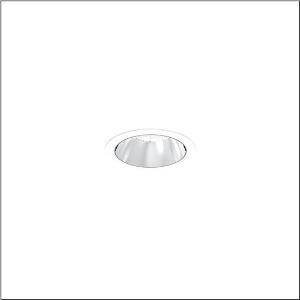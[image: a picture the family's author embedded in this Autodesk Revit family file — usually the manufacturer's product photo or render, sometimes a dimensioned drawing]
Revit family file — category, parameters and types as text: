
# Revit family: lunis_21_m_51db15ec91c
name_source: partatom
category: Lighting Fixtures
units: mm (PartAtom-declared; Revit-internal decimal feet)

## family parameters
Cut with Voids When Loaded = No
Host = Face
Light Source = No
Part Type = Normal
Room Calculation Point = No
Round Connector Dimension = Use Diameter
Shared = No

## types (1)
- --- (1 x LED, 3950 lm, 25.5 W, 4000K)
    Apparent Load = 26 VA
    CIE Flux Codes = 95 100 100 100 100
    Color Rendering = 80
    Color Temperature = 4000K
    Default Elevation = 1800 mm
    Description = Lunis 21,  M, downlight, light control with lens, of PMMA, anti glare with reflector, of PC, highly specular, light emission: direct distribution, LED rated luminous flux: 1.820lm, light colour: 830/840/865, with terminal, 5-pole, mains connection: 220..240V, AC/DC, 0/50..60Hz, housing, round, of diecast aluminium, traffic white (RAL 9016), diameter: 115mm, clamping range: 1..40mm, protection rating (complete): IP20, protection rating (on room side): IP54, insulation class (complete): insulation class II (safety insulation), certification: CE, impact resistance: IK03, packaging unit: 1 piece
    Height = 0 mm  [stored 0 ft]
    Lamp = 1 x LED
    Lamp Light Flux = 3950 lm
    Lamp Power = 25.5 W
    Lamp count = 1
    Length = 115 mm
    Luminous efficacy = 155 lm/W
    Manufacturer = Siteco
    ModVariant = No
    Model = 51DB15EC91C
    Mounting Place = Ceiling
    Mounting Type = Recessed
    Number of Poles = 1
    OnlyDefault = Yes
    Power Factor = 1
    Product Name = Lunis 21 M
    Product group = downlight
    ProductGroupID = 400
    Protection Class = Protection class II
    Protection Degree = IP 20
    RLX_Detail_Level = 1
    RLX_Emergency_Light_Flux = 0 lm
    RLX_Emergency_Type = 0
    RLX_Emergency_Type_DB = No
    RlxData = <blob elided: 11329 chars, md5=64ab8428>
    Socket = socket
    Standby Power = 0 W
    System Light Flux = 3950 lm
    System Power = 26 W
    Type Comments = individual setting: colour temperature 4000K, luminous flux: 100 % | (ON | ON | OFF | OFF) | 700 mA
    Type Image = l_1290850.jpg
    URL = http://relux.com
    VarID = @adj_017723
    Voltage = 0 V
    Weight = 0.00 kg
    Width = 0 mm  [stored 0 ft]

note: [stored X ft] marks values corroborated as IEEE doubles in the binary element streams (Revit-internal decimal feet)

## geometry (parser evidence)
native form markers: Sweep x10
no freeform markers — native parametric forms only
